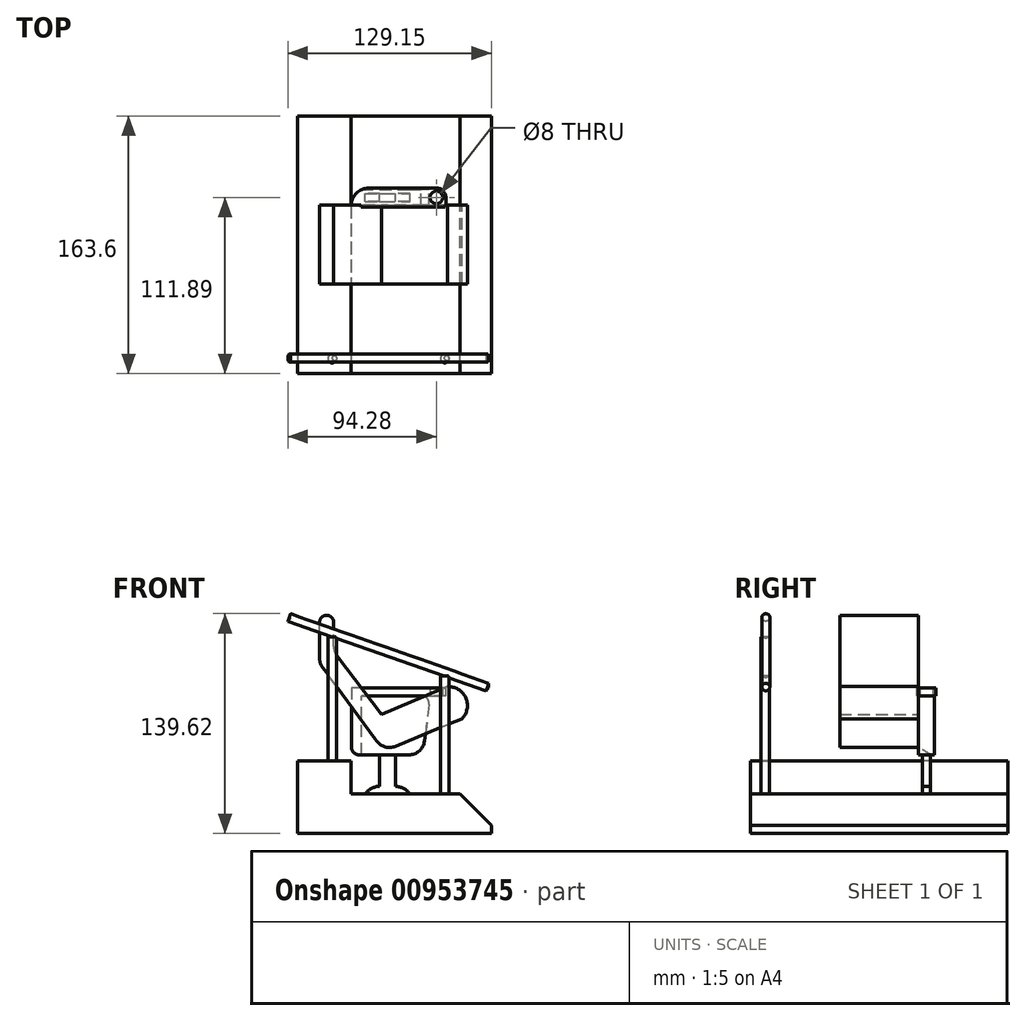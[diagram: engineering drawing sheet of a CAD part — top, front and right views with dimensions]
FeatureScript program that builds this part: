
annotation { "Feature Type Name" : "Feature", "Feature Type Description" : "" }
export const myFeature = defineFeature(function(context is Context, id is Id, definition is map)
    precondition{}
    {
        {
            var Q0;
            Q0=qCreatedBy(makeId("Front.planeOp"),FACE);
            var sketch = newSketch(context, id + "F0", { "sketchPlane" : qUnion([Q0])});
            skLineSegment(sketch, "E0", {"start": v(0, 0) * mm, "end": v(50, 0) * mm});
            skLineSegment(sketch, "E1", {"start": v(0, -37.56) * mm, "end": v(45.37, -37.56) * mm});
            skLineSegment(sketch, "E2", {"start": v(0, 0) * mm, "end": v(0, -37.56) * mm});
            skLineSegment(sketch, "E3", {"start": v(50, 0) * mm, "end": v(45.37, -37.56) * mm});
            skSolve(sketch);
        }
        {
            var Q0;
            Q0 = qSketchRegion(id + "F0", true);
            extrude(context, id + "F1", {"entities" : qUnion([Q0]), "endBound" : BoundingType.SYMMETRIC, "depth" : 10 * mm, "offsetDistance" : 25 * mm});
        }
        {
            var Q0;
            Q0=makeQuery(id+"F1.opExtrude","SWEPT_EDGE",EDGE,{"disambiguationData":[OSD([sQuery(id+"F0.wireOp",EDGE,"E1"),sQuery(id+"F0.wireOp",EDGE,"E2")])]});
            var Q1;
            Q1=makeQuery(id+"F1.opExtrude","SWEPT_EDGE",EDGE,{"disambiguationData":[OSD([sQuery(id+"F0.wireOp",EDGE,"E0"),sQuery(id+"F0.wireOp",EDGE,"E3")])]});
            fillet(context, id + "F2", {"entities" : qUnion([Q0, Q1]), "radius" : 5 * mm, "tangentPropagation" : true, "allowEdgeOverflow" : false});
        }
        {
            var Q0;
            Q0=makeQuery(id+"F1.opExtrude","SWEPT_EDGE",EDGE,{"disambiguationData":[OSD([sQuery(id+"F0.wireOp",EDGE,"E1"),sQuery(id+"F0.wireOp",EDGE,"E3")])]});
            fillet(context, id + "F3", {"entities" : qUnion([Q0]), "radius" : 10 * mm, "tangentPropagation" : true, "allowEdgeOverflow" : false});
        }
        {
            var Q0;
            Q0=qCreatedBy(makeId("Front.planeOp"),FACE);
            var sketch = newSketch(context, id + "F4", { "sketchPlane" : qUnion([Q0])});
            skLineSegment(sketch, "E4.0", {"start": v(18.04, -37.56) * mm, "end": v(28.04, -37.56) * mm});
            skLineSegment(sketch, "E5.top", {"start": v(18.04, -57.56) * mm, "end": v(28.04, -57.56) * mm});
            skLineSegment(sketch, "E5.left", {"start": v(18.04, -37.56) * mm, "end": v(18.04, -57.56) * mm});
            skLineSegment(sketch, "E5.right", {"start": v(28.04, -37.56) * mm, "end": v(28.04, -57.56) * mm});
            skLineSegment(sketch, "E6.top", {"start": v(8.74, -62.56) * mm, "end": v(37.24, -62.56) * mm});
            skArc(sketch, "E7", {"start": v(18.04, -57.56) * mm, "mid": v(12.76, -58.9) * mm, "end": v(8.74, -62.56) * mm});
            skArc(sketch, "E8", {"start": v(37.24, -62.56) * mm, "mid": v(33.26, -58.92) * mm, "end": v(28.04, -57.56) * mm});
            skSolve(sketch);
        }
        {
            var Q0;
            Q0 = qSketchRegion(id + "F4", true);
            extrude(context, id + "F5", {"entities" : qUnion([Q0]), "operationType" : NewBodyOperationType.ADD, "endBound" : BoundingType.SYMMETRIC, "depth" : 5 * mm, "offsetDistance" : 25 * mm});
        }
        {
            var Q0;
            Q0=makeQuery(id+"F1.opExtrude","CAP_FACE",FACE,{"disambiguationData":[OSD([sQuery(id+"F0.wireOp",EDGE,"E0"),sQuery(id+"F0.wireOp",EDGE,"E1"),sQuery(id+"F0.wireOp",EDGE,"E2"),sQuery(id+"F0.wireOp",EDGE,"E3")])],"isStart":false});
            var sketch = newSketch(context, id + "F6", { "sketchPlane" : qUnion([Q0])});
            skLineSegment(sketch, "E9", {"start": v(61.21, 5.76) * mm, "end": v(19.01, -11.73) * mm});
            skLineSegment(sketch, "E10", {"start": v(15.1, -27.33) * mm, "end": v(-20.23, 20.64) * mm});
            skLineSegment(sketch, "E11", {"start": v(-11.23, 28.04) * mm, "end": v(19.01, -11.73) * mm});
            skLineSegment(sketch, "E12", {"start": v(-11.23, 28.04) * mm, "end": v(-11.23, 36.63) * mm});
            skLineSegment(sketch, "E13", {"start": v(-20.23, 20.64) * mm, "end": v(-20.23, 36.63) * mm});
            skLineSegment(sketch, "E14", {"start": v(15.1, -27.33) * mm, "end": v(20.76, -35.14) * mm});
            skPoint(sketch, "E14.endSnap0", {"position": v(20.76, -37.56) * mm});
            skLineSegment(sketch, "E15", {"start": v(20.76, -35.14) * mm, "end": v(70.33, -14.58) * mm});
            skArc(sketch, "E16", {"start": v(70.33, -14.58) * mm, "mid": v(72.67, -1.32) * mm, "end": v(61.21, 5.76) * mm});
            skLineSegment(sketch, "E17.top", {"start": v(-11.23, 46.63) * mm, "end": v(-20.23, 46.63) * mm});
            skLineSegment(sketch, "E17.left", {"start": v(-11.23, 36.63) * mm, "end": v(-11.23, 46.63) * mm});
            skLineSegment(sketch, "E17.right", {"start": v(-20.23, 36.63) * mm, "end": v(-20.23, 46.63) * mm});
            skCircle(sketch, "E18", {"center": v(-15.73, 46.63) * mm, "radius": 4.5 * mm});
            skSolve(sketch);
        }
        {
            var Q0;
            Q0 = qSketchRegion(id + "F6", true);
            extrude(context, id + "F7", {"entities" : qUnion([Q0]), "operationType" : NewBodyOperationType.ADD, "depth" : 50 * mm, "offsetDistance" : 25 * mm});
        }
        {
            var Q0;
            Q0=makeQuery(id+"F7.opExtrude","SWEPT_EDGE",EDGE,{"disambiguationData":[OSD([sQuery(id+"F6.wireOp",EDGE,"E14"),sQuery(id+"F6.wireOp",EDGE,"E15")])]});
            fillet(context, id + "F8", {"entities" : qUnion([Q0]), "radius" : 10 * mm, "tangentPropagation" : true, "allowEdgeOverflow" : false});
        }
        {
            var Q0;
            Q0=qCreatedBy(makeId("Top.planeOp"),FACE);
            var sketch = newSketch(context, id + "F9", { "sketchPlane" : qUnion([Q0])});
            skLineSegment(sketch, "E19.bottom", {"start": v(0, 6) * mm, "end": v(60, 6) * mm});
            skLineSegment(sketch, "E19.top", {"start": v(0, -6) * mm, "end": v(60, -6) * mm});
            skLineSegment(sketch, "E19.left", {"start": v(0, 6) * mm, "end": v(0, -6) * mm});
            skLineSegment(sketch, "E19.right", {"start": v(60, 6) * mm, "end": v(60, -6) * mm});
            skSolve(sketch);
        }
        {
            var Q0;
            Q0 = qSketchRegion(id + "F9", true);
            extrude(context, id + "F10", {"entities" : qUnion([Q0]), "operationType" : NewBodyOperationType.ADD, "depth" : 5 * mm, "offsetDistance" : 25 * mm});
        }
        {
            var Q0;
            Q0=makeQuery(id+"F10.opExtrude","SWEPT_EDGE",EDGE,{"disambiguationData":[OSD([sQuery(id+"F9.wireOp",EDGE,"E19.bottom"),sQuery(id+"F9.wireOp",EDGE,"E19.right")])]});
            fillet(context, id + "F11", {"entities" : qUnion([Q0]), "radius" : 6 * mm, "tangentPropagation" : true, "allowEdgeOverflow" : false});
        }
        {
            var Q0;
            Q0=makeQuery(id+"F10.opExtrude","SWEPT_EDGE",EDGE,{"disambiguationData":[OSD([sQuery(id+"F9.wireOp",EDGE,"E19.bottom"),sQuery(id+"F9.wireOp",EDGE,"E19.left")])]});
            fillet(context, id + "F12", {"entities" : qUnion([Q0]), "radius" : 11 * mm, "tangentPropagation" : true, "allowEdgeOverflow" : false});
        }
        {
            var Q0;
            Q0=qCreatedBy(makeId("Top.planeOp"),FACE);
            var sketch = newSketch(context, id + "F13", { "sketchPlane" : qUnion([Q0])});
            skPoint(sketch, "E20", {"position": v(54, 0) * mm});
            skSolve(sketch);
        }
        {
            var Q0;
            Q0=sQuery(id+"F13.wireOp",VERTEX,"E20");
            var Q1;
            Q1=makeQuery(id+"F1.opExtrude","SWEPT_BODY",BODY,{"disambiguationData":[OSD([sQuery(id+"F0.wireOp",EDGE,"E0"),sQuery(id+"F0.wireOp",EDGE,"E1"),sQuery(id+"F0.wireOp",EDGE,"E2"),sQuery(id+"F0.wireOp",EDGE,"E3")])]});
            hole(context, id + "F14", {"style" : HoleStyle.SIMPLE, "endStyle" : HoleEndStyle.THROUGH, "oppositeDirection" : true, "holeDiameter" : 8 * mm, "majorDiameter" : 5 * mm, "isTappedThrough" : true, "tappedDepth" : 12 * mm, "tapClearance" : 3, "locations" : qUnion([Q0]), "scope" : qUnion([Q1])});
        }
        {
            var Q0;
            Q0=qCreatedBy(makeId("Front.planeOp"),FACE);
            cPlane(context, id + "F15", {"entities" : qUnion([Q0]), "cplaneType" : CPlaneType.OFFSET, "offset" : 30 * mm, "width" : 150 * mm, "height" : 150 * mm});
        }
        {
            var Q0;
            Q0=makeQuery(id+"F7.opExtrude","SWEPT_EDGE",EDGE,{"disambiguationData":[OSD([sQuery(id+"F6.wireOp",EDGE,"E10"),sQuery(id+"F6.wireOp",EDGE,"E13")])]});
            fillet(context, id + "F16", {"entities" : qUnion([Q0]), "radius" : 10 * mm, "tangentPropagation" : true, "allowEdgeOverflow" : false});
        }
        {
            var Q0;
            Q0=makeQuery(id+"F7.opExtrude","SWEPT_EDGE",EDGE,{"disambiguationData":[OSD([sQuery(id+"F6.wireOp",EDGE,"E11"),sQuery(id+"F6.wireOp",EDGE,"E12")])]});
            fillet(context, id + "F17", {"entities" : qUnion([Q0]), "radius" : 10 * mm, "tangentPropagation" : true, "allowEdgeOverflow" : false});
        }
        {
            var Q0;
            Q0=qCreatedBy(makeId("Top.planeOp"),FACE);
            cPlane(context, id + "F18", {"entities" : qUnion([Q0]), "cplaneType" : CPlaneType.OFFSET, "offset" : 62.5 * mm, "oppositeDirection" : true, "width" : 150 * mm, "height" : 150 * mm});
        }
        {
            var Q0;
            Q0=qCreatedBy(id+"F18.planeOp",FACE);
            var sketch = newSketch(context, id + "F19", { "sketchPlane" : qUnion([Q0])});
            skLineSegment(sketch, "E21.bottom", {"start": v(88.87, 51.71) * mm, "end": v(-34.25, 51.71) * mm});
            skLineSegment(sketch, "E21.top", {"start": v(88.87, -111.89) * mm, "end": v(-34.25, -111.89) * mm});
            skLineSegment(sketch, "E21.left", {"start": v(88.87, 51.71) * mm, "end": v(88.87, -111.89) * mm});
            skLineSegment(sketch, "E21.right", {"start": v(-34.25, 51.71) * mm, "end": v(-34.25, -111.89) * mm});
            skPoint(sketch, "E21.middle", {"position": v(27.31, -30.09) * mm});
            skSolve(sketch);
        }
        {
            var Q0;
            Q0 = qSketchRegion(id + "F19", true);
            extrude(context, id + "F20", {"entities" : qUnion([Q0]), "oppositeDirection" : true, "depth" : 25 * mm, "offsetDistance" : 25 * mm});
        }
        {
            var Q0;
            Q0=makeQuery(id+"F20.opExtrude","CAP_EDGE",EDGE,{"disambiguationData":[OSD([sQuery(id+"F19.wireOp",EDGE,"E21.left")])],"isStart":true});
            chamfer(context, id + "F21", {"entities" : qUnion([Q0]), "width" : 20 * mm, "tangentPropagation" : true});
        }
        {
            var Q0;
            Q0=makeQuery(id+"F20.opExtrude","CAP_EDGE",EDGE,{"disambiguationData":[OSD([sQuery(id+"F19.wireOp",EDGE,"E21.top")])],"isStart":true});
            cPoint(context, id + "F22", {"entities" : qUnion([Q0]), "parameter" : 0.5});
        }
        {
            var Q0;
            Q0=makeQuery(id+"F20.opExtrude","CAP_VERTEX",VERTEX,{"disambiguationData":[OSD([sQuery(id+"F19.wireOp",EDGE,"E21.top"),sQuery(id+"F19.wireOp",EDGE,"E21.right")])],"isStart":true});
            var Q1;
            Q1=makeQuery(id+"F20.opExtrude","CAP_VERTEX",VERTEX,{"disambiguationData":[OSD([sQuery(id+"F19.wireOp",EDGE,"E21.top"),sQuery(id+"F19.wireOp",EDGE,"E21.right")])],"isStart":false});
            var Q2;
            Q2 = qCreatedBy(id + "F22" ,VERTEX);
            cPlane(context, id + "F23", {"entities" : qUnion([Q0, Q1, Q2]), "cplaneType" : CPlaneType.THREE_POINT, "offset" : 25 * mm, "width" : 150 * mm, "height" : 150 * mm});
        }
        {
            var Q0;
            Q0=qCreatedBy(id+"F23.planeOp",FACE);
            var sketch = newSketch(context, id + "F24", { "sketchPlane" : qUnion([Q0])});
            skLineSegment(sketch, "E22.0", {"start": v(0.25, -62.5) * mm, "end": v(34.25, -62.5) * mm});
            skLineSegment(sketch, "E23.bottom", {"start": v(34.25, -62.5) * mm, "end": v(0.25, -62.5) * mm});
            skLineSegment(sketch, "E23.top", {"start": v(34.25, -41.43) * mm, "end": v(0.25, -41.43) * mm});
            skLineSegment(sketch, "E23.left", {"start": v(34.25, -62.5) * mm, "end": v(34.25, -41.43) * mm});
            skLineSegment(sketch, "E23.right", {"start": v(0.25, -62.5) * mm, "end": v(0.25, -41.43) * mm});
            skPoint(sketch, "E24.0.end.orphan", {"position": v(0.25, -62.5) * mm});
            skSolve(sketch);
        }
        {
            var Q0;
            Q0 = qSketchRegion(id + "F24", true);
            extrude(context, id + "F25", {"entities" : qUnion([Q0]), "operationType" : NewBodyOperationType.ADD, "depth" : 163.6 * mm, "offsetDistance" : 25 * mm});
        }
        {
            var Q0;
            Q0=qCreatedBy(id+"F15.planeOp",FACE);
            cPlane(context, id + "F26", {"entities" : qUnion([Q0]), "cplaneType" : CPlaneType.OFFSET, "offset" : 72 * mm, "width" : 150 * mm, "height" : 150 * mm});
        }
        {
            var Q0;
            Q0=makeQuery(id+"F20.opExtrude","CAP_EDGE",EDGE,{"disambiguationData":[OSD([sQuery(id+"F19.wireOp",EDGE,"E21.top")])],"isStart":false});
            cPlane(context, id + "F27", {"entities" : qUnion([Q0]), "cplaneType" : CPlaneType.LINE_ANGLE, "offset" : 0 * mm, "angle" : 90 * degree, "width" : 150 * mm, "height" : 150 * mm});
        }
        {
            var Q0;
            Q0=qCreatedBy(id+"F27.planeOp",FACE);
            var sketch = newSketch(context, id + "F28", { "sketchPlane" : qUnion([Q0])});
            skLineSegment(sketch, "E25", {"start": v(56.64, -102.38) * mm, "end": v(59.33, -102.38) * mm});
            skLineSegment(sketch, "E26", {"start": v(-14.93, -102.38) * mm, "end": v(-12.18, -102.38) * mm});
            skSolve(sketch);
        }
        {
            var Q0;
            Q0=sQuery(id+"F28.wireOp",EDGE,"E25");
            extrude(context, id + "F29", {"bodyType" : ToolBodyType.SURFACE, "surfaceEntities" : qUnion([Q0]), "depth" : 100 * mm, "offsetDistance" : 25 * mm});
        }
        {
            var Q0;
            Q0=makeQuery(id+"F29.opExtrude","SWEPT_FACE",FACE,{"disambiguationData":[OSD([sQuery(id+"F28.wireOp",EDGE,"E25")])]});
            var Q1;
            Q1=makeQuery(id+"F29.opExtrude","SWEPT_EDGE",EDGE,{"disambiguationData":[OSD([sQuery(id+"F28.wireOp",VERTEX,"E25.end")])]});
            revolve(context, id + "F30", {"operationType" : NewBodyOperationType.ADD, "surfaceOperationType" : NewSurfaceOperationType.NEW, "entities" : qUnion([Q0]), "axis" : qUnion([Q1]), "revolveType" : RevolveType.FULL});
        }
        {
            var Q0;
            Q0=sQuery(id+"F28.wireOp",EDGE,"E26");
            extrude(context, id + "F31", {"bodyType" : ToolBodyType.SURFACE, "surfaceEntities" : qUnion([Q0]), "depth" : 125 * mm, "offsetDistance" : 25 * mm});
        }
        {
            var Q0;
            Q0=makeQuery(id+"F31.opExtrude","SWEPT_FACE",FACE,{"disambiguationData":[OSD([sQuery(id+"F28.wireOp",EDGE,"E26")])]});
            var Q1;
            Q1=makeQuery(id+"F31.opExtrude","SWEPT_EDGE",EDGE,{"disambiguationData":[OSD([sQuery(id+"F28.wireOp",VERTEX,"E26.end")])]});
            revolve(context, id + "F32", {"operationType" : NewBodyOperationType.ADD, "surfaceOperationType" : NewSurfaceOperationType.NEW, "entities" : qUnion([Q0]), "axis" : qUnion([Q1]), "revolveType" : RevolveType.FULL});
        }
        {
            var Q0;
            Q0=qCreatedBy(id+"F26.planeOp",FACE);
            var sketch = newSketch(context, id + "F33", { "sketchPlane" : qUnion([Q0])});
            skLineSegment(sketch, "E27", {"start": v(-38.6, 49.43) * mm, "end": v(87.22, 5.23) * mm});
            skLineSegment(sketch, "E28", {"start": v(87.22, 7.92) * mm, "end": v(-38.6, 52.12) * mm});
            skLineSegment(sketch, "E29", {"start": v(-38.6, 52.12) * mm, "end": v(-38.6, 49.43) * mm});
            skLineSegment(sketch, "E30", {"start": v(87.22, 5.23) * mm, "end": v(87.22, 7.92) * mm});
            skSolve(sketch);
        }
        {
            var Q0;
            Q0=makeQuery(id+"F33.imprint","IMPRINT",FACE,{"disambiguationData":[TD([[makeQuery(id+"F33.imprint","IMPRINT",EDGE,{"derivedFrom":sQuery(id+"F33.wireOp",EDGE,"E27")}),1.0]])]});
            var Q1;
            Q1=sQuery(id+"F33.wireOp",EDGE,"E27");
            revolve(context, id + "F34", {"operationType" : NewBodyOperationType.ADD, "surfaceOperationType" : NewSurfaceOperationType.NEW, "entities" : qUnion([Q0]), "axis" : qUnion([Q1]), "revolveType" : RevolveType.FULL});
        }
    });
